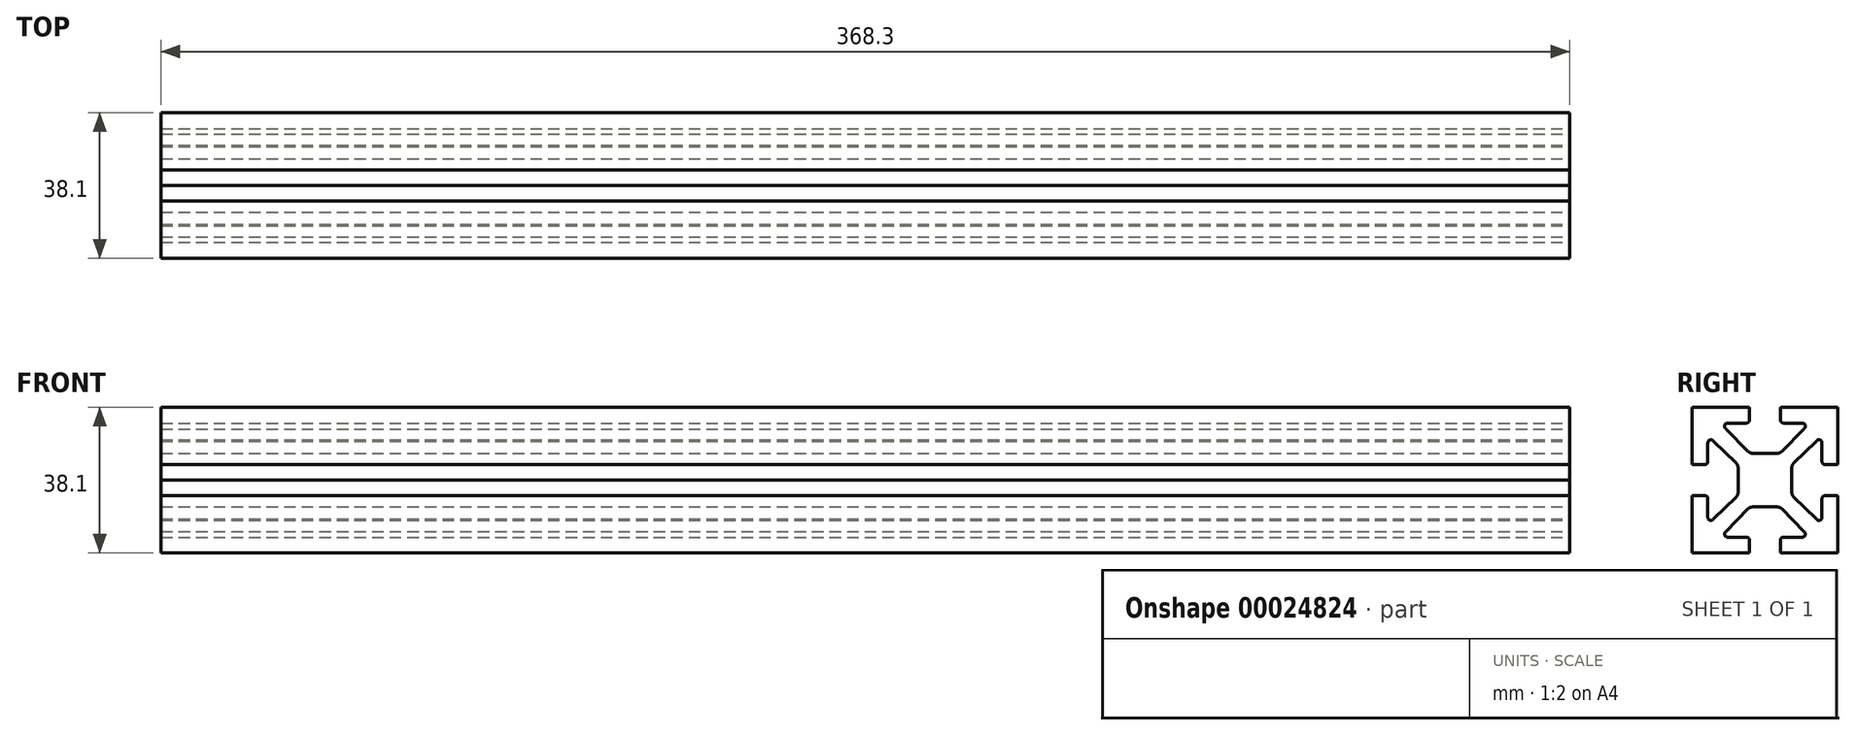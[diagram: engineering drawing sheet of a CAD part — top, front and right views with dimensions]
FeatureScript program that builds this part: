
annotation { "Feature Type Name" : "Feature", "Feature Type Description" : "" }
export const myFeature = defineFeature(function(context is Context, id is Id, definition is map)
    precondition{}
    {
        {
            var Q0;
            Q0=qCreatedBy(makeId("Right.planeOp"),FACE);
            var sketch = newSketch(context, id + "F0", { "sketchPlane" : qUnion([Q0])});
            skLineSegment(sketch, "E0.rect.bottom", {"start": v(19.05, 19.05) * mm, "end": v(-19.05, 19.05) * mm});
            skLineSegment(sketch, "E0.rect.top", {"start": v(19.05, -19.05) * mm, "end": v(-19.05, -19.05) * mm});
            skLineSegment(sketch, "E0.rect.left", {"start": v(19.05, 19.05) * mm, "end": v(19.05, -19.05) * mm});
            skLineSegment(sketch, "E0.rect.right", {"start": v(-19.05, 19.05) * mm, "end": v(-19.05, -19.05) * mm});
            skPoint(sketch, "E0.rect.middle", {"position": v(0, 0) * mm});
            skSolve(sketch);
        }
        {
            var Q0;
            Q0=makeQuery(id+"F0.imprint","IMPRINT",FACE,{"disambiguationData":[TD([[makeQuery(id+"F0.imprint","IMPRINT",EDGE,{"derivedFrom":sQuery(id+"F0.wireOp",EDGE,"E0.rect.bottom")}),1.0]])]});
            extrude(context, id + "F1", {"entities" : qUnion([Q0]), "endBound" : BoundingType.SYMMETRIC, "depth" : 368.3 * mm});
        }
        {
            var Q0;
            Q0=qCreatedBy(makeId("Right.planeOp"),FACE);
            var sketch = newSketch(context, id + "F2", { "sketchPlane" : qUnion([Q0])});
            skLineSegment(sketch, "E1", {"start": v(-4.06, 19.11) * mm, "end": v(-4.06, 15.71) * mm});
            skLineSegment(sketch, "E2", {"start": v(-4.86, 14.92) * mm, "end": v(-9.78, 14.92) * mm});
            skLineSegment(sketch, "E3", {"start": v(0, 6.99) * mm, "end": v(0, 19.05) * mm});
            skLineSegment(sketch, "E4", {"start": v(0, 19.05) * mm, "end": v(-4.06, 19.11) * mm});
            skPoint(sketch, "E5.visualSharp", {"position": v(-10.29, 14.92) * mm});
            skArc(sketch, "E5.filletArc", {"start": v(-9.78, 14.92) * mm, "mid": v(-10.56, 14.3) * mm, "end": v(-10.12, 13.4) * mm});
            skPoint(sketch, "E6.visualSharp", {"position": v(-4.06, 14.92) * mm});
            skArc(sketch, "E6.filletArc", {"start": v(-4.86, 14.92) * mm, "mid": v(-4.3, 15.15) * mm, "end": v(-4.06, 15.71) * mm});
            skLineSegment(sketch, "E7", {"start": v(-10.12, 13.4) * mm, "end": v(-4.4, 7.51) * mm});
            skLineSegment(sketch, "E8", {"start": v(-3.28, 7.03) * mm, "end": v(0, 6.99) * mm});
            skPoint(sketch, "E9.visualSharp", {"position": v(-3.94, 7.04) * mm});
            skArc(sketch, "E9.filletArc", {"start": v(-4.4, 7.51) * mm, "mid": v(-3.89, 7.16) * mm, "end": v(-3.28, 7.03) * mm});
            skLineSegment(sketch, "E10.1.0", {"start": v(6.99, 0) * mm, "end": v(19.05, 0) * mm});
            skArc(sketch, "E10.1.1", {"start": v(7.51, 4.4) * mm, "mid": v(7.16, 3.89) * mm, "end": v(7.03, 3.28) * mm});
            skLineSegment(sketch, "E10.1.2", {"start": v(14.92, 4.86) * mm, "end": v(14.92, 9.78) * mm});
            skLineSegment(sketch, "E10.1.3", {"start": v(19.11, 4.06) * mm, "end": v(15.71, 4.06) * mm});
            skLineSegment(sketch, "E10.1.4", {"start": v(19.05, 0) * mm, "end": v(19.11, 4.06) * mm});
            skLineSegment(sketch, "E10.1.5", {"start": v(7.03, 3.28) * mm, "end": v(6.99, 0) * mm});
            skLineSegment(sketch, "E10.1.6", {"start": v(13.4, 10.12) * mm, "end": v(7.51, 4.4) * mm});
            skArc(sketch, "E10.1.7", {"start": v(14.92, 4.86) * mm, "mid": v(15.15, 4.3) * mm, "end": v(15.71, 4.06) * mm});
            skArc(sketch, "E10.1.8", {"start": v(14.92, 9.78) * mm, "mid": v(14.3, 10.56) * mm, "end": v(13.4, 10.12) * mm});
            skLineSegment(sketch, "E10.2.0", {"start": v(0, -6.99) * mm, "end": v(0, -19.05) * mm});
            skArc(sketch, "E10.2.1", {"start": v(4.4, -7.51) * mm, "mid": v(3.89, -7.16) * mm, "end": v(3.28, -7.03) * mm});
            skLineSegment(sketch, "E10.2.2", {"start": v(4.86, -14.92) * mm, "end": v(9.78, -14.92) * mm});
            skLineSegment(sketch, "E10.2.3", {"start": v(4.06, -19.11) * mm, "end": v(4.06, -15.71) * mm});
            skLineSegment(sketch, "E10.2.4", {"start": v(0, -19.05) * mm, "end": v(4.06, -19.11) * mm});
            skLineSegment(sketch, "E10.2.5", {"start": v(3.28, -7.03) * mm, "end": v(0, -6.99) * mm});
            skLineSegment(sketch, "E10.2.6", {"start": v(10.12, -13.4) * mm, "end": v(4.4, -7.51) * mm});
            skArc(sketch, "E10.2.7", {"start": v(4.86, -14.92) * mm, "mid": v(4.3, -15.15) * mm, "end": v(4.06, -15.71) * mm});
            skArc(sketch, "E10.2.8", {"start": v(9.78, -14.92) * mm, "mid": v(10.56, -14.3) * mm, "end": v(10.12, -13.4) * mm});
            skPoint(sketch, "E10.center", {"position": v(0, 0) * mm});
            skLineSegment(sketch, "E10.anchor1", {"start": v(0, 0) * mm, "end": v(-10.12, 13.4) * mm, "construction": true});
            skLineSegment(sketch, "E10.anchor2", {"start": v(0, 0) * mm, "end": v(-13.4, -10.12) * mm, "construction": true});
            skArc(sketch, "E11.3.3.0", {"start": v(-7.51, -4.4) * mm, "mid": v(-7.16, -3.89) * mm, "end": v(-7.03, -3.28) * mm});
            skLineSegment(sketch, "E11.7.3.0", {"start": v(-14.92, -4.86) * mm, "end": v(-14.92, -9.78) * mm});
            skLineSegment(sketch, "E11.10.3.0", {"start": v(-19.11, -4.06) * mm, "end": v(-15.71, -4.06) * mm});
            skLineSegment(sketch, "E11.13.3.0", {"start": v(-19.05, 0) * mm, "end": v(-19.11, -4.06) * mm});
            skLineSegment(sketch, "E11.16.3.0", {"start": v(-7.03, -3.28) * mm, "end": v(-6.99, 0) * mm});
            skLineSegment(sketch, "E11.19.3.0", {"start": v(-13.4, -10.12) * mm, "end": v(-7.51, -4.4) * mm});
            skLineSegment(sketch, "E11.20.3.0", {"start": v(-6.99, 0) * mm, "end": v(-19.05, 0) * mm});
            skArc(sketch, "E11.22.3.0", {"start": v(-14.92, -4.86) * mm, "mid": v(-15.15, -4.3) * mm, "end": v(-15.71, -4.06) * mm});
            skArc(sketch, "E11.26.3.0", {"start": v(-14.92, -9.78) * mm, "mid": v(-14.3, -10.56) * mm, "end": v(-13.4, -10.12) * mm});
            skSolve(sketch);
        }
        {
            var Q0;
            Q0 = qSketchRegion(id + "F2", true);
            extrude(context, id + "F3", {"entities" : qUnion([Q0]), "operationType" : NewBodyOperationType.REMOVE, "endBound" : BoundingType.SYMMETRIC, "oppositeDirection" : true, "depth" : 368.3 * mm});
        }
        {
            var Q0;
            Q0=makeQuery(id+"F1.opExtrude","SWEPT_BODY",BODY,{"disambiguationData":[OSD([sQuery(id+"F0.wireOp",EDGE,"E0.rect.bottom"),sQuery(id+"F0.wireOp",EDGE,"E0.rect.top"),sQuery(id+"F0.wireOp",EDGE,"E0.rect.left"),sQuery(id+"F0.wireOp",EDGE,"E0.rect.right")])]});
            var Q1;
            Q1=qCreatedBy(makeId("Front.planeOp"),FACE);
            mirror(context, id + "F4", {"operationType" : NewBodyOperationType.INTERSECT, "entities" : qUnion([Q0]), "mirrorPlane" : qUnion([Q1])});
        }
    });
